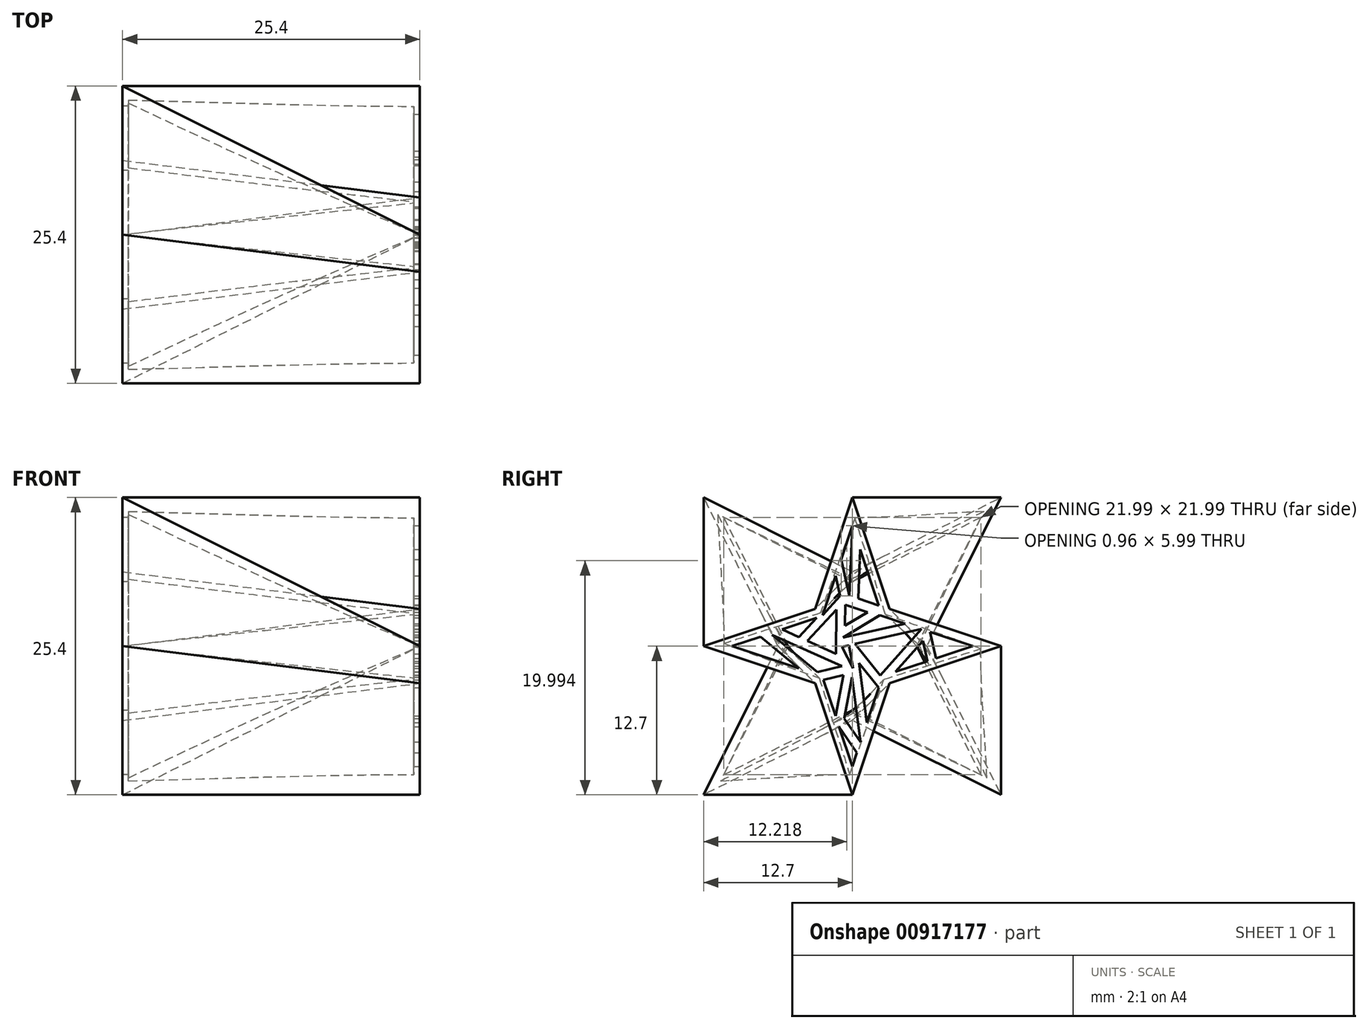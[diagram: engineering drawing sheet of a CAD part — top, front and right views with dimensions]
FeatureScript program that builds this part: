
annotation { "Feature Type Name" : "Feature", "Feature Type Description" : "" }
export const myFeature = defineFeature(function(context is Context, id is Id, definition is map)
    precondition{}
    {
        {
            var Q0;
            Q0=qCreatedBy(makeId("Right.planeOp"),FACE);
            var sketch = newSketch(context, id + "F0", { "sketchPlane" : qUnion([Q0])});
            skLineSegment(sketch, "E0.bottom", {"start": v(12.7, -12.7) * mm, "end": v(-12.7, -12.7) * mm});
            skLineSegment(sketch, "E0.top", {"start": v(12.7, 12.7) * mm, "end": v(-12.7, 12.7) * mm});
            skLineSegment(sketch, "E0.left", {"start": v(12.7, -12.7) * mm, "end": v(12.7, 12.7) * mm});
            skLineSegment(sketch, "E0.right", {"start": v(-12.7, -12.7) * mm, "end": v(-12.7, 12.7) * mm});
            skPoint(sketch, "E0.middle", {"position": v(0, 0) * mm});
            skLineSegment(sketch, "E1", {"start": v(0, 6.35) * mm, "end": v(12.7, 12.7) * mm});
            skLineSegment(sketch, "E2", {"start": v(12.7, 12.7) * mm, "end": v(6.35, 0) * mm});
            skLineSegment(sketch, "E3", {"start": v(6.35, 0) * mm, "end": v(12.7, -12.7) * mm});
            skLineSegment(sketch, "E4", {"start": v(12.7, -12.7) * mm, "end": v(0, -6.35) * mm});
            skLineSegment(sketch, "E5", {"start": v(0, -6.35) * mm, "end": v(-12.7, -12.7) * mm});
            skLineSegment(sketch, "E6", {"start": v(-12.7, -12.7) * mm, "end": v(-6.35, 0) * mm});
            skLineSegment(sketch, "E7", {"start": v(-6.35, 0) * mm, "end": v(-12.7, 12.7) * mm});
            skLineSegment(sketch, "E8", {"start": v(0, 6.35) * mm, "end": v(-12.7, 12.7) * mm});
            skSolve(sketch);
        }
        {
            var Q0;
            Q0=makeQuery(id+"F0.imprint","IMPRINT",FACE,{"disambiguationData":[TD([[makeQuery(id+"F0.imprint","IMPRINT",EDGE,{"derivedFrom":sQuery(id+"F0.wireOp",EDGE,"E1")}),-1.0]])]});
            cPlane(context, id + "F1", {"entities" : qUnion([Q0]), "cplaneType" : CPlaneType.OFFSET, "offset" : 25.4 * mm, "width" : 152.4 * mm, "height" : 152.4 * mm});
        }
        {
            var Q0;
            Q0=qCreatedBy(id+"F1.planeOp",FACE);
            var sketch = newSketch(context, id + "F2", { "sketchPlane" : qUnion([Q0])});
            skLineSegment(sketch, "E9", {"start": v(-10.3, 0) * mm, "end": v(-4.58, -1.9) * mm});
            skLineSegment(sketch, "E10", {"start": v(-4.58, -1.9) * mm, "end": v(-7.86, 0.81) * mm});
            skLineSegment(sketch, "E11", {"start": v(-7.86, 0.81) * mm, "end": v(-10.3, 0) * mm});
            skLineSegment(sketch, "E12", {"start": v(-2.99, -2.23) * mm, "end": v(-6.84, 0.96) * mm});
            skLineSegment(sketch, "E13", {"start": v(-6.84, 0.96) * mm, "end": v(-0.89, -1.7) * mm});
            skLineSegment(sketch, "E14", {"start": v(-0.89, -1.7) * mm, "end": v(-2.99, -2.23) * mm});
            skLineSegment(sketch, "E15", {"start": v(-3.05, 2.41) * mm, "end": v(-6.01, 1.43) * mm});
            skLineSegment(sketch, "E16", {"start": v(-6.01, 1.43) * mm, "end": v(-4.56, 0.78) * mm});
            skLineSegment(sketch, "E17", {"start": v(-4.56, 0.78) * mm, "end": v(-3.05, 2.41) * mm});
            skLineSegment(sketch, "E18", {"start": v(-1.39, -0.65) * mm, "end": v(-3.83, 0.45) * mm});
            skLineSegment(sketch, "E19", {"start": v(-3.83, 0.45) * mm, "end": v(-1.38, 3.1) * mm});
            skLineSegment(sketch, "E20", {"start": v(-1.38, 3.1) * mm, "end": v(-1.39, -0.65) * mm});
            skLineSegment(sketch, "E21", {"start": v(-0.77, -2.46) * mm, "end": v(-2.47, -2.89) * mm});
            skLineSegment(sketch, "E22", {"start": v(-2.47, -2.89) * mm, "end": v(-1.44, -5.97) * mm});
            skLineSegment(sketch, "E23", {"start": v(-1.44, -5.97) * mm, "end": v(-0.77, -2.46) * mm});
            skLineSegment(sketch, "E24", {"start": v(-1.13, -6.89) * mm, "end": v(0, -10.3) * mm});
            skLineSegment(sketch, "E25", {"start": v(0, -10.3) * mm, "end": v(0.4, -9.1) * mm});
            skLineSegment(sketch, "E26", {"start": v(0.4, -9.1) * mm, "end": v(-1.13, -6.89) * mm});
            skLineSegment(sketch, "E27", {"start": v(0.7, -8.19) * mm, "end": v(-0.7, -6.17) * mm});
            skLineSegment(sketch, "E28", {"start": v(-0.7, -6.17) * mm, "end": v(-0.03, -2.65) * mm});
            skLineSegment(sketch, "E29", {"start": v(-0.03, -2.65) * mm, "end": v(0.7, -8.19) * mm});
            skLineSegment(sketch, "E30", {"start": v(1.25, -6.54) * mm, "end": v(0.58, -1.47) * mm});
            skLineSegment(sketch, "E31", {"start": v(0.58, -1.47) * mm, "end": v(2.25, -3.55) * mm});
            skLineSegment(sketch, "E32", {"start": v(2.25, -3.55) * mm, "end": v(1.25, -6.54) * mm});
            skLineSegment(sketch, "E33", {"start": v(6.43, -1.29) * mm, "end": v(3.7, -2.2) * mm});
            skLineSegment(sketch, "E34", {"start": v(3.7, -2.2) * mm, "end": v(6.04, 0.44) * mm});
            skLineSegment(sketch, "E35", {"start": v(6.04, 0.44) * mm, "end": v(6.43, -1.29) * mm});
            skLineSegment(sketch, "E36", {"start": v(2.4, -2.52) * mm, "end": v(5.92, 1.46) * mm});
            skLineSegment(sketch, "E37", {"start": v(5.92, 1.46) * mm, "end": v(0.23, 0.19) * mm});
            skLineSegment(sketch, "E38", {"start": v(0.23, 0.19) * mm, "end": v(2.4, -2.52) * mm});
            skLineSegment(sketch, "E39", {"start": v(6.64, 1.22) * mm, "end": v(7.16, -1.04) * mm});
            skLineSegment(sketch, "E40", {"start": v(7.16, -1.04) * mm, "end": v(10.3, 0) * mm});
            skLineSegment(sketch, "E41", {"start": v(10.3, 0) * mm, "end": v(6.64, 1.22) * mm});
            skLineSegment(sketch, "E42", {"start": v(4.51, 1.93) * mm, "end": v(2.35, 2.65) * mm});
            skLineSegment(sketch, "E43", {"start": v(2.35, 2.65) * mm, "end": v(-0.8, 0.74) * mm});
            skLineSegment(sketch, "E44", {"start": v(-0.8, 0.74) * mm, "end": v(4.51, 1.93) * mm});
            skLineSegment(sketch, "E45", {"start": v(2.27, 3.48) * mm, "end": v(0.68, 8.26) * mm});
            skLineSegment(sketch, "E46", {"start": v(0.68, 8.26) * mm, "end": v(0.5, 4.07) * mm});
            skLineSegment(sketch, "E47", {"start": v(0.5, 4.07) * mm, "end": v(2.27, 3.48) * mm});
            skLineSegment(sketch, "E48", {"start": v(-0.62, 1.74) * mm, "end": v(1.3, 2.9) * mm});
            skLineSegment(sketch, "E49", {"start": v(-0.61, 3.54) * mm, "end": v(-0.62, 1.74) * mm});
            skLineSegment(sketch, "E50", {"start": v(-0.61, 3.54) * mm, "end": v(1.3, 2.9) * mm});
            skLineSegment(sketch, "E51", {"start": v(0, 10.3) * mm, "end": v(-0.96, 7.4) * mm});
            skLineSegment(sketch, "E52", {"start": v(-0.96, 7.4) * mm, "end": v(-0.25, 4.3) * mm});
            skLineSegment(sketch, "E53", {"start": v(-0.25, 4.3) * mm, "end": v(0, 10.3) * mm});
            skLineSegment(sketch, "E54", {"start": v(-2.55, 2.65) * mm, "end": v(-1.03, 4.3) * mm});
            skLineSegment(sketch, "E55", {"start": v(-1.03, 4.3) * mm, "end": v(-1.43, 6) * mm});
            skLineSegment(sketch, "E56", {"start": v(-1.43, 6) * mm, "end": v(-2.55, 2.65) * mm});
            skLineSegment(sketch, "E57", {"start": v(0.07, -1.9) * mm, "end": v(-0.88, -0.06) * mm});
            skLineSegment(sketch, "E58", {"start": v(-0.88, -0.06) * mm, "end": v(-0.28, 0.08) * mm});
            skLineSegment(sketch, "E59", {"start": v(-0.28, 0.08) * mm, "end": v(0.07, -1.9) * mm});
            skSolve(sketch);
        }
        {
            var Q0;
            Q0=qCreatedBy(id+"F1.planeOp",FACE);
            var sketch = newSketch(context, id + "F3", { "sketchPlane" : qUnion([Q0])});
            skLineSegment(sketch, "E60", {"start": v(-12.7, 0) * mm, "end": v(-3.17, -3.17) * mm});
            skLineSegment(sketch, "E61", {"start": v(-3.17, -3.17) * mm, "end": v(0, -12.7) * mm});
            skLineSegment(sketch, "E62", {"start": v(0, -12.7) * mm, "end": v(3.17, -3.17) * mm});
            skLineSegment(sketch, "E63", {"start": v(3.17, -3.17) * mm, "end": v(12.7, 0) * mm});
            skLineSegment(sketch, "E64", {"start": v(12.7, 0) * mm, "end": v(3.17, 3.17) * mm});
            skLineSegment(sketch, "E65", {"start": v(3.17, 3.17) * mm, "end": v(0, 12.7) * mm});
            skLineSegment(sketch, "E66", {"start": v(0, 12.7) * mm, "end": v(-3.17, 3.17) * mm});
            skLineSegment(sketch, "E67", {"start": v(-3.17, 3.17) * mm, "end": v(-12.7, 0) * mm});
            skSolve(sketch);
        }
        {
            var Q0;
            Q0=makeQuery(id+"F0.imprint","IMPRINT",FACE,{"disambiguationData":[TD([[makeQuery(id+"F0.imprint","IMPRINT",EDGE,{"derivedFrom":sQuery(id+"F0.wireOp",EDGE,"E1")}),-1.0]])]});
            var Q1;
            Q1=makeQuery(id+"F3.imprint","IMPRINT",FACE,{"disambiguationData":[TD([[makeQuery(id+"F3.imprint","IMPRINT",EDGE,{"derivedFrom":sQuery(id+"F3.wireOp",EDGE,"E60")}),1.0]])]});
            loft(context, id + "F4", {"sheetProfilesArray" : [{ "sheetProfileEntities" : qUnion([Q0]) }, { "sheetProfileEntities" : qUnion([Q1]) }]});
        }
        {
            var Q0;
            Q0=makeQuery(id+"F4.opLoft","CAP_FACE",FACE,{"disambiguationData":[OSD([makeQuery(id+"F3.imprint","IMPRINT",FACE,{"disambiguationData":[TD([[makeQuery(id+"F3.imprint","IMPRINT",EDGE,{"derivedFrom":sQuery(id+"F3.wireOp",EDGE,"E60")}),1.0]])]})])],"isStart":true});
            var Q1;
            Q1=makeQuery(id+"F4.opLoft","SWEPT_BODY",BODY,{"disambiguationData":[OSD([makeQuery(id+"F0.imprint","IMPRINT",FACE,{"disambiguationData":[TD([[makeQuery(id+"F0.imprint","IMPRINT",EDGE,{"derivedFrom":sQuery(id+"F0.wireOp",EDGE,"E1")}),-1.0]])]}),makeQuery(id+"F3.imprint","IMPRINT",FACE,{"disambiguationData":[TD([[makeQuery(id+"F3.imprint","IMPRINT",EDGE,{"derivedFrom":sQuery(id+"F3.wireOp",EDGE,"E60")}),1.0]])]})])]});
            shell(context, id + "F5", {"isHollow" : true, "entities" : qUnion([Q0]), "parts" : qUnion([Q1]), "thickness" : 0.5 * mm});
        }
        {
            var Q0;
            Q0=makeQuery(id+"F2.imprint","IMPRINT",FACE,{"disambiguationData":[TD([[makeQuery(id+"F2.imprint","IMPRINT",EDGE,{"derivedFrom":sQuery(id+"F2.wireOp",EDGE,"E51")}),1.0]])]});
            var Q1;
            Q1=makeQuery(id+"F2.imprint","IMPRINT",FACE,{"disambiguationData":[TD([[makeQuery(id+"F2.imprint","IMPRINT",EDGE,{"derivedFrom":sQuery(id+"F2.wireOp",EDGE,"E45")}),1.0]])]});
            var Q2;
            Q2=makeQuery(id+"F2.imprint","IMPRINT",FACE,{"disambiguationData":[TD([[makeQuery(id+"F2.imprint","IMPRINT",EDGE,{"derivedFrom":sQuery(id+"F2.wireOp",EDGE,"E39")}),1.0]])]});
            var Q3;
            Q3=makeQuery(id+"F2.imprint","IMPRINT",FACE,{"disambiguationData":[TD([[makeQuery(id+"F2.imprint","IMPRINT",EDGE,{"derivedFrom":sQuery(id+"F2.wireOp",EDGE,"E48")}),1.0]])]});
            var Q4;
            Q4=makeQuery(id+"F2.imprint","IMPRINT",FACE,{"disambiguationData":[TD([[makeQuery(id+"F2.imprint","IMPRINT",EDGE,{"derivedFrom":sQuery(id+"F2.wireOp",EDGE,"E42")}),1.0]])]});
            var Q5;
            Q5=makeQuery(id+"F2.imprint","IMPRINT",FACE,{"disambiguationData":[TD([[makeQuery(id+"F2.imprint","IMPRINT",EDGE,{"derivedFrom":sQuery(id+"F2.wireOp",EDGE,"E36")}),1.0]])]});
            var Q6;
            Q6=makeQuery(id+"F2.imprint","IMPRINT",FACE,{"disambiguationData":[TD([[makeQuery(id+"F2.imprint","IMPRINT",EDGE,{"derivedFrom":sQuery(id+"F2.wireOp",EDGE,"E54")}),1.0]])]});
            var Q7;
            Q7=makeQuery(id+"F2.imprint","IMPRINT",FACE,{"disambiguationData":[TD([[makeQuery(id+"F2.imprint","IMPRINT",EDGE,{"derivedFrom":sQuery(id+"F2.wireOp",EDGE,"E33")}),-1.0]])]});
            var Q8;
            Q8=makeQuery(id+"F2.imprint","IMPRINT",FACE,{"disambiguationData":[TD([[makeQuery(id+"F2.imprint","IMPRINT",EDGE,{"derivedFrom":sQuery(id+"F2.wireOp",EDGE,"E18")}),-1.0]])]});
            var Q9;
            Q9=makeQuery(id+"F2.imprint","IMPRINT",FACE,{"disambiguationData":[TD([[makeQuery(id+"F2.imprint","IMPRINT",EDGE,{"derivedFrom":sQuery(id+"F2.wireOp",EDGE,"E15")}),1.0]])]});
            var Q10;
            Q10=makeQuery(id+"F2.imprint","IMPRINT",FACE,{"disambiguationData":[TD([[makeQuery(id+"F2.imprint","IMPRINT",EDGE,{"derivedFrom":sQuery(id+"F2.wireOp",EDGE,"E57")}),-1.0]])]});
            var Q11;
            Q11=makeQuery(id+"F2.imprint","IMPRINT",FACE,{"disambiguationData":[TD([[makeQuery(id+"F2.imprint","IMPRINT",EDGE,{"derivedFrom":sQuery(id+"F2.wireOp",EDGE,"E9")}),1.0]])]});
            var Q12;
            Q12=makeQuery(id+"F2.imprint","IMPRINT",FACE,{"disambiguationData":[TD([[makeQuery(id+"F2.imprint","IMPRINT",EDGE,{"derivedFrom":sQuery(id+"F2.wireOp",EDGE,"E30")}),-1.0]])]});
            var Q13;
            Q13=makeQuery(id+"F2.imprint","IMPRINT",FACE,{"disambiguationData":[TD([[makeQuery(id+"F2.imprint","IMPRINT",EDGE,{"derivedFrom":sQuery(id+"F2.wireOp",EDGE,"E12")}),-1.0]])]});
            var Q14;
            Q14=makeQuery(id+"F2.imprint","IMPRINT",FACE,{"disambiguationData":[TD([[makeQuery(id+"F2.imprint","IMPRINT",EDGE,{"derivedFrom":sQuery(id+"F2.wireOp",EDGE,"E21")}),1.0]])]});
            var Q15;
            Q15=makeQuery(id+"F2.imprint","IMPRINT",FACE,{"disambiguationData":[TD([[makeQuery(id+"F2.imprint","IMPRINT",EDGE,{"derivedFrom":sQuery(id+"F2.wireOp",EDGE,"E27")}),-1.0]])]});
            var Q16;
            Q16=makeQuery(id+"F2.imprint","IMPRINT",FACE,{"disambiguationData":[TD([[makeQuery(id+"F2.imprint","IMPRINT",EDGE,{"derivedFrom":sQuery(id+"F2.wireOp",EDGE,"E24")}),1.0]])]});
            extrude(context, id + "F6", {"entities" : qUnion([Q0, Q1, Q2, Q3, Q4, Q5, Q6, Q7, Q8, Q9, Q10, Q11, Q12, Q13, Q14, Q15, Q16]), "operationType" : NewBodyOperationType.REMOVE, "endBound" : BoundingType.UP_TO_NEXT, "oppositeDirection" : true, "depth" : 0.5 * mm, "offsetDistance" : 25.4 * mm});
        }
        {
            var Q0;
            Q0=makeQuery(id+"F0.imprint","IMPRINT",FACE,{"disambiguationData":[TD([[makeQuery(id+"F0.imprint","IMPRINT",EDGE,{"derivedFrom":sQuery(id+"F0.wireOp",EDGE,"E1")}),-1.0]])]});
            var sketch = newSketch(context, id + "F7", { "sketchPlane" : qUnion([Q0])});
            skLineSegment(sketch, "E68", {"start": v(5.5, 0) * mm, "end": v(11, 11) * mm});
            skLineSegment(sketch, "E69", {"start": v(11, 11) * mm, "end": v(0, 5.5) * mm});
            skLineSegment(sketch, "E70", {"start": v(0, 5.5) * mm, "end": v(-11, 11) * mm});
            skLineSegment(sketch, "E71", {"start": v(-11, 11) * mm, "end": v(-5.5, 0) * mm});
            skLineSegment(sketch, "E72", {"start": v(-5.5, 0) * mm, "end": v(-11, -11) * mm});
            skLineSegment(sketch, "E73", {"start": v(-11, -11) * mm, "end": v(0, -5.5) * mm});
            skLineSegment(sketch, "E74", {"start": v(0, -5.5) * mm, "end": v(11, -11) * mm});
            skLineSegment(sketch, "E75", {"start": v(11, -11) * mm, "end": v(5.5, 0) * mm});
            skSolve(sketch);
        }
        {
            var Q0;
            Q0 = qSketchRegion(id + "F7", true);
            extrude(context, id + "F8", {"entities" : qUnion([Q0]), "operationType" : NewBodyOperationType.REMOVE, "endBound" : BoundingType.UP_TO_NEXT, "depth" : 25.4 * mm, "offsetDistance" : 25.4 * mm});
        }
    });
